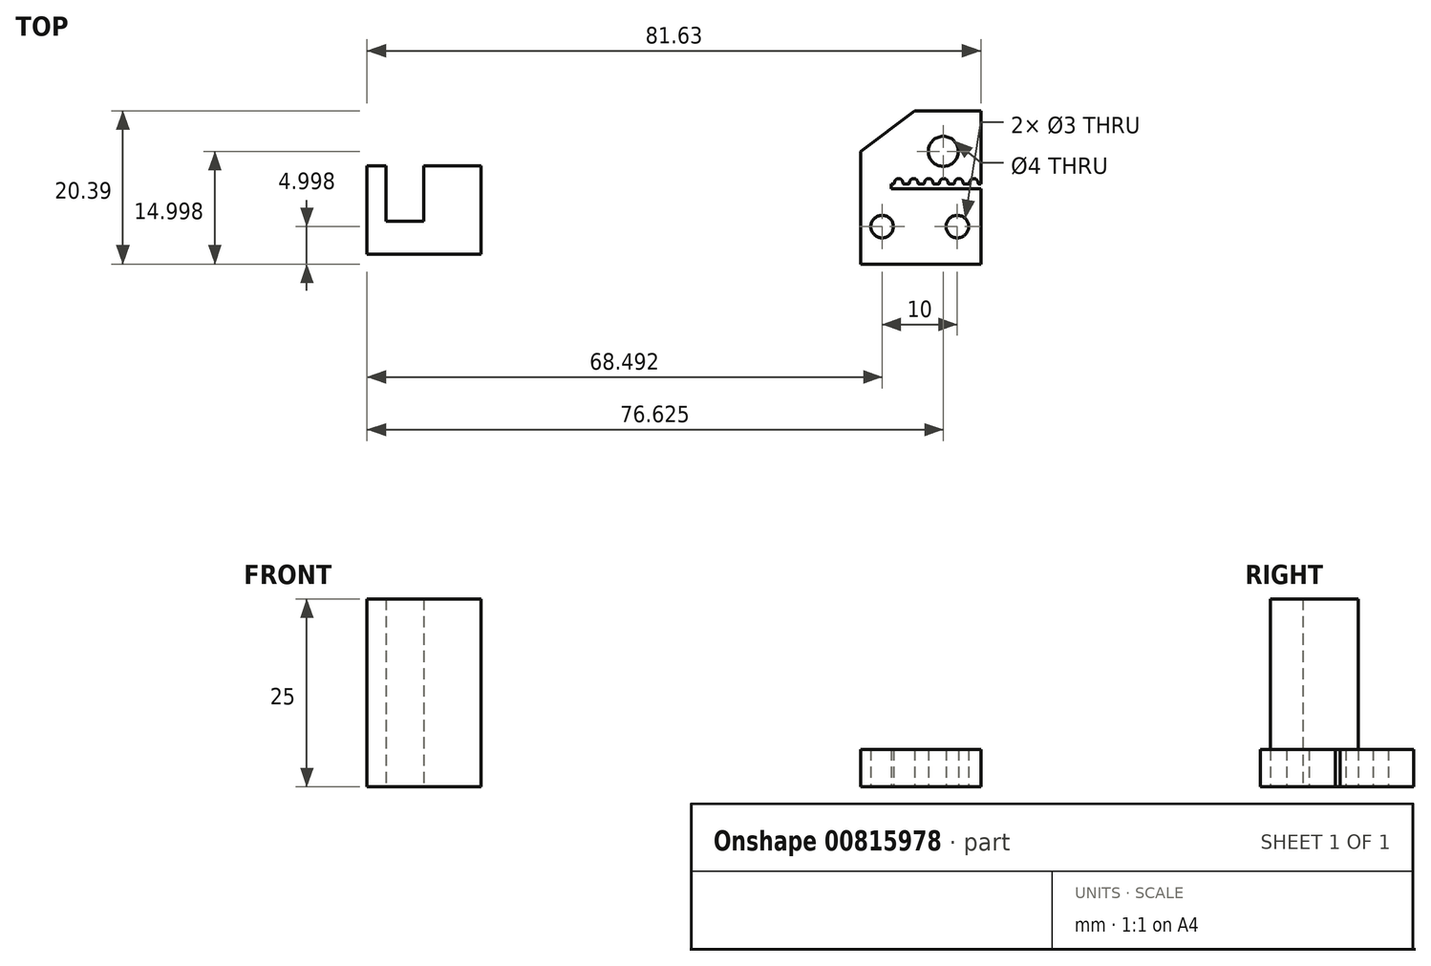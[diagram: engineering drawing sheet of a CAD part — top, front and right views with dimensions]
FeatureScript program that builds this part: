
annotation { "Feature Type Name" : "Feature", "Feature Type Description" : "" }
export const myFeature = defineFeature(function(context is Context, id is Id, definition is map)
    precondition{}
    {
        {
            var Q0;
            Q0=qCreatedBy(makeId("Top.planeOp"),FACE);
            var sketch = newSketch(context, id + "F0", { "sketchPlane" : qUnion([Q0])});
            skLineSegment(sketch, "E0.bottom", {"start": v(-41.36, 24.94) * mm, "end": v(38.64, 24.94) * mm});
            skLineSegment(sketch, "E0.top", {"start": v(-41.36, 74.94) * mm, "end": v(38.64, 74.94) * mm});
            skLineSegment(sketch, "E0.left", {"start": v(-41.36, 24.94) * mm, "end": v(-41.36, 74.94) * mm});
            skLineSegment(sketch, "E0.right", {"start": v(38.64, 24.94) * mm, "end": v(38.64, 74.94) * mm});
            skCircle(sketch, "E1", {"center": v(-21.36, 70.94) * mm, "radius": 1.37 * mm});
            skCircle(sketch, "E2", {"center": v(-21.36, 64.94) * mm, "radius": 1.5 * mm});
            skCircle(sketch, "E3", {"center": v(-11.36, 70.94) * mm, "radius": 1.5 * mm});
            skCircle(sketch, "E4", {"center": v(-11.36, 64.94) * mm, "radius": 1.5 * mm});
            skCircle(sketch, "E5", {"center": v(-1.36, 70.94) * mm, "radius": 1.5 * mm});
            skCircle(sketch, "E6", {"center": v(-1.36, 64.94) * mm, "radius": 1.5 * mm});
            skCircle(sketch, "E7", {"center": v(8.64, 70.94) * mm, "radius": 1.5 * mm});
            skCircle(sketch, "E8", {"center": v(8.64, 64.94) * mm, "radius": 1.5 * mm});
            skCircle(sketch, "E9", {"center": v(18.64, 70.94) * mm, "radius": 1.5 * mm});
            skCircle(sketch, "E10", {"center": v(18.64, 64.94) * mm, "radius": 1.5 * mm});
            skCircle(sketch, "E11", {"center": v(-21.36, 28.94) * mm, "radius": 1.5 * mm});
            skCircle(sketch, "E12", {"center": v(-11.36, 28.94) * mm, "radius": 1.5 * mm});
            skCircle(sketch, "E13", {"center": v(-1.36, 28.94) * mm, "radius": 1.5 * mm});
            skCircle(sketch, "E14", {"center": v(8.64, 28.94) * mm, "radius": 1.5 * mm});
            skCircle(sketch, "E15", {"center": v(18.64, 28.94) * mm, "radius": 1.5 * mm});
            skCircle(sketch, "E16", {"center": v(-11.36, 57.94) * mm, "radius": 1.5 * mm});
            skCircle(sketch, "E17", {"center": v(8.64, 57.94) * mm, "radius": 1.5 * mm});
            skCircle(sketch, "E18", {"center": v(-11.36, 37.94) * mm, "radius": 1.5 * mm});
            skCircle(sketch, "E19", {"center": v(8.64, 37.94) * mm, "radius": 1.5 * mm});
            skCircle(sketch, "E20", {"center": v(33.64, 62.94) * mm, "radius": 2 * mm});
            skCircle(sketch, "E21", {"center": v(35.5, 52.94) * mm, "radius": 1.5 * mm});
            skCircle(sketch, "E22", {"center": v(35.5, 42.94) * mm, "radius": 1.5 * mm});
            skCircle(sketch, "E23", {"center": v(25.5, 52.94) * mm, "radius": 1.5 * mm});
            skCircle(sketch, "E24", {"center": v(25.5, 42.94) * mm, "radius": 1.5 * mm});
            skCircle(sketch, "E25", {"center": v(33.84, 32.94) * mm, "radius": 2 * mm});
            skLineSegment(sketch, "E26", {"start": v(37.7, 57.94) * mm, "end": v(38.7, 57.94) * mm});
            skLineSegment(sketch, "E27", {"start": v(38.7, 57.94) * mm, "end": v(38.7, 58.57) * mm});
            skArc(sketch, "E28", {"start": v(38.2, 59) * mm, "mid": v(37.99, 59.23) * mm, "end": v(37.7, 59.32) * mm});
            skArc(sketch, "E29", {"start": v(38.29, 58.7) * mm, "mid": v(38.25, 58.86) * mm, "end": v(38.2, 59) * mm});
            skArc(sketch, "E30", {"start": v(38.29, 58.7) * mm, "mid": v(38.34, 58.6) * mm, "end": v(38.44, 58.57) * mm});
            skLineSegment(sketch, "E31", {"start": v(38.44, 58.57) * mm, "end": v(38.7, 58.57) * mm});
            skArc(sketch, "E32.0.MirrorCS", {"start": v(37.2, 59) * mm, "mid": v(37.4, 59.23) * mm, "end": v(37.7, 59.32) * mm});
            skArc(sketch, "E33.0.MirrorCS", {"start": v(37.1, 58.7) * mm, "mid": v(37.14, 58.86) * mm, "end": v(37.2, 59) * mm});
            skArc(sketch, "E34.0.MirrorCS", {"start": v(37.1, 58.7) * mm, "mid": v(37.05, 58.6) * mm, "end": v(36.96, 58.57) * mm});
            skLineSegment(sketch, "E35.0.MirrorCS", {"start": v(36.96, 58.57) * mm, "end": v(36.7, 58.57) * mm});
            skLineSegment(sketch, "E36.0.MirrorCS", {"start": v(36.7, 57.94) * mm, "end": v(36.7, 58.57) * mm});
            skLineSegment(sketch, "E37.0.MirrorCS", {"start": v(37.7, 57.94) * mm, "end": v(36.7, 57.94) * mm});
            skArc(sketch, "E38.MirrorCS", {"start": v(35.2, 59) * mm, "mid": v(35.4, 59.23) * mm, "end": v(35.7, 59.32) * mm});
            skArc(sketch, "E39.MirrorCS", {"start": v(36.2, 59) * mm, "mid": v(35.99, 59.23) * mm, "end": v(35.7, 59.32) * mm});
            skArc(sketch, "E40.MirrorCS", {"start": v(36.29, 58.7) * mm, "mid": v(36.25, 58.86) * mm, "end": v(36.2, 59) * mm});
            skArc(sketch, "E41.MirrorCS", {"start": v(36.29, 58.7) * mm, "mid": v(36.34, 58.6) * mm, "end": v(36.44, 58.57) * mm});
            skLineSegment(sketch, "E42.MirrorCS", {"start": v(36.44, 58.57) * mm, "end": v(36.7, 58.57) * mm});
            skArc(sketch, "E43.MirrorCS", {"start": v(35.1, 58.7) * mm, "mid": v(35.14, 58.86) * mm, "end": v(35.2, 59) * mm});
            skArc(sketch, "E44.MirrorCS", {"start": v(35.1, 58.7) * mm, "mid": v(35.05, 58.6) * mm, "end": v(34.96, 58.57) * mm});
            skLineSegment(sketch, "E45.MirrorCS", {"start": v(34.96, 58.57) * mm, "end": v(34.7, 58.57) * mm});
            skLineSegment(sketch, "E46.MirrorCS", {"start": v(34.7, 57.94) * mm, "end": v(34.7, 58.57) * mm});
            skLineSegment(sketch, "E47.MirrorCS", {"start": v(35.7, 57.94) * mm, "end": v(36.7, 57.94) * mm});
            skLineSegment(sketch, "E48.MirrorCS", {"start": v(35.7, 57.94) * mm, "end": v(34.7, 57.94) * mm});
            skLineSegment(sketch, "E49.MirrorCS", {"start": v(34.44, 58.57) * mm, "end": v(34.7, 58.57) * mm});
            skArc(sketch, "E50.MirrorCS", {"start": v(34.29, 58.7) * mm, "mid": v(34.34, 58.6) * mm, "end": v(34.44, 58.57) * mm});
            skArc(sketch, "E51.MirrorCS", {"start": v(34.29, 58.7) * mm, "mid": v(34.25, 58.86) * mm, "end": v(34.2, 59) * mm});
            skArc(sketch, "E52.MirrorCS", {"start": v(34.2, 59) * mm, "mid": v(33.99, 59.23) * mm, "end": v(33.7, 59.32) * mm});
            skArc(sketch, "E53.MirrorCS", {"start": v(33.2, 59) * mm, "mid": v(33.4, 59.23) * mm, "end": v(33.7, 59.32) * mm});
            skArc(sketch, "E54.MirrorCS", {"start": v(33.1, 58.7) * mm, "mid": v(33.14, 58.86) * mm, "end": v(33.2, 59) * mm});
            skArc(sketch, "E55.MirrorCS", {"start": v(33.1, 58.7) * mm, "mid": v(33.05, 58.6) * mm, "end": v(32.96, 58.57) * mm});
            skLineSegment(sketch, "E56.MirrorCS", {"start": v(32.96, 58.57) * mm, "end": v(32.7, 58.57) * mm});
            skLineSegment(sketch, "E57.MirrorCS", {"start": v(32.44, 58.57) * mm, "end": v(32.7, 58.57) * mm});
            skArc(sketch, "E58.MirrorCS", {"start": v(32.29, 58.7) * mm, "mid": v(32.34, 58.6) * mm, "end": v(32.44, 58.57) * mm});
            skArc(sketch, "E59.MirrorCS", {"start": v(32.29, 58.7) * mm, "mid": v(32.25, 58.86) * mm, "end": v(32.2, 59) * mm});
            skArc(sketch, "E60.MirrorCS", {"start": v(32.2, 59) * mm, "mid": v(31.99, 59.23) * mm, "end": v(31.7, 59.32) * mm});
            skArc(sketch, "E61.MirrorCS", {"start": v(31.2, 59) * mm, "mid": v(31.4, 59.23) * mm, "end": v(31.7, 59.32) * mm});
            skArc(sketch, "E62.MirrorCS", {"start": v(31.1, 58.7) * mm, "mid": v(31.14, 58.86) * mm, "end": v(31.2, 59) * mm});
            skArc(sketch, "E63.MirrorCS", {"start": v(31.1, 58.7) * mm, "mid": v(31.05, 58.6) * mm, "end": v(30.96, 58.57) * mm});
            skLineSegment(sketch, "E64.MirrorCS", {"start": v(30.96, 58.57) * mm, "end": v(30.7, 58.57) * mm});
            skLineSegment(sketch, "E65.MirrorCS", {"start": v(30.7, 57.94) * mm, "end": v(30.7, 58.57) * mm});
            skLineSegment(sketch, "E66.MirrorCS", {"start": v(31.7, 57.94) * mm, "end": v(30.7, 57.94) * mm});
            skLineSegment(sketch, "E67.MirrorCS", {"start": v(31.7, 57.94) * mm, "end": v(32.7, 57.94) * mm});
            skLineSegment(sketch, "E68.MirrorCS", {"start": v(33.7, 57.94) * mm, "end": v(32.7, 57.94) * mm});
            skLineSegment(sketch, "E69.MirrorCS", {"start": v(33.7, 57.94) * mm, "end": v(34.7, 57.94) * mm});
            skLineSegment(sketch, "E70.MirrorCS", {"start": v(29.7, 57.94) * mm, "end": v(30.7, 57.94) * mm});
            skLineSegment(sketch, "E71.MirrorCS", {"start": v(29.7, 57.94) * mm, "end": v(28.7, 57.94) * mm});
            skLineSegment(sketch, "E72.MirrorCS", {"start": v(27.7, 57.94) * mm, "end": v(28.7, 57.94) * mm});
            skLineSegment(sketch, "E73.MirrorCS", {"start": v(27.7, 57.94) * mm, "end": v(26.7, 57.94) * mm});
            skLineSegment(sketch, "E74.MirrorCS", {"start": v(26.7, 57.94) * mm, "end": v(26.7, 58.57) * mm});
            skLineSegment(sketch, "E75.MirrorCS", {"start": v(30.44, 58.57) * mm, "end": v(30.7, 58.57) * mm});
            skArc(sketch, "E76.MirrorCS", {"start": v(30.29, 58.7) * mm, "mid": v(30.34, 58.6) * mm, "end": v(30.44, 58.57) * mm});
            skArc(sketch, "E77.MirrorCS", {"start": v(30.29, 58.7) * mm, "mid": v(30.25, 58.86) * mm, "end": v(30.2, 59) * mm});
            skArc(sketch, "E78.MirrorCS", {"start": v(30.2, 59) * mm, "mid": v(29.99, 59.23) * mm, "end": v(29.7, 59.32) * mm});
            skArc(sketch, "E79.MirrorCS", {"start": v(29.2, 59) * mm, "mid": v(29.4, 59.23) * mm, "end": v(29.7, 59.32) * mm});
            skArc(sketch, "E80.MirrorCS", {"start": v(29.1, 58.7) * mm, "mid": v(29.14, 58.86) * mm, "end": v(29.2, 59) * mm});
            skArc(sketch, "E81.MirrorCS", {"start": v(29.1, 58.7) * mm, "mid": v(29.05, 58.6) * mm, "end": v(28.96, 58.57) * mm});
            skLineSegment(sketch, "E82.MirrorCS", {"start": v(28.96, 58.57) * mm, "end": v(28.7, 58.57) * mm});
            skLineSegment(sketch, "E83.MirrorCS", {"start": v(28.44, 58.57) * mm, "end": v(28.7, 58.57) * mm});
            skArc(sketch, "E84.MirrorCS", {"start": v(28.29, 58.7) * mm, "mid": v(28.34, 58.6) * mm, "end": v(28.44, 58.57) * mm});
            skArc(sketch, "E85.MirrorCS", {"start": v(28.29, 58.7) * mm, "mid": v(28.25, 58.86) * mm, "end": v(28.2, 59) * mm});
            skArc(sketch, "E86.MirrorCS", {"start": v(28.2, 59) * mm, "mid": v(27.99, 59.23) * mm, "end": v(27.7, 59.32) * mm});
            skArc(sketch, "E87.MirrorCS", {"start": v(27.2, 59) * mm, "mid": v(27.4, 59.23) * mm, "end": v(27.7, 59.32) * mm});
            skArc(sketch, "E88.MirrorCS", {"start": v(27.1, 58.7) * mm, "mid": v(27.14, 58.86) * mm, "end": v(27.2, 59) * mm});
            skArc(sketch, "E89.MirrorCS", {"start": v(27.1, 58.7) * mm, "mid": v(27.05, 58.6) * mm, "end": v(26.96, 58.57) * mm});
            skLineSegment(sketch, "E90.MirrorCS", {"start": v(26.96, 58.57) * mm, "end": v(26.7, 58.57) * mm});
            skPoint(sketch, "E91", {"position": v(38.64, 47.94) * mm});
            skLineSegment(sketch, "E92", {"start": v(38.64, 47.94) * mm, "end": v(22.64, 47.94) * mm});
            skLineSegment(sketch, "E93", {"start": v(22.64, 47.94) * mm, "end": v(22.64, 62.94) * mm});
            skLineSegment(sketch, "E94", {"start": v(22.64, 62.94) * mm, "end": v(38.64, 74.94) * mm});
            skLineSegment(sketch, "E95", {"start": v(29.83, 68.33) * mm, "end": v(38.64, 68.33) * mm});
            skSolve(sketch);
        }
        {
            var Q0;
            Q0=makeQuery(id+"F0.imprint","IMPRINT",FACE,{"disambiguationData":[TD([[makeQuery(id+"F0.imprint","IMPRINT",EDGE,{"derivedFrom":sQuery(id+"F0.wireOp",EDGE,"E20")}),-1.0]])]});
            extrude(context, id + "F1", {"entities" : qUnion([Q0]), "depth" : 5 * mm, "offsetDistance" : 25 * mm});
        }
        {
            var Q0;
            Q0=qCreatedBy(makeId("Top.planeOp"),FACE);
            var sketch = newSketch(context, id + "F2", { "sketchPlane" : qUnion([Q0])});
            skLineSegment(sketch, "E96.bottom", {"start": v(-42.99, 60.98) * mm, "end": v(-27.85, 60.98) * mm});
            skLineSegment(sketch, "E96.top", {"start": v(-42.99, 49.3) * mm, "end": v(-27.85, 49.3) * mm});
            skLineSegment(sketch, "E96.left", {"start": v(-42.99, 60.98) * mm, "end": v(-42.99, 49.3) * mm});
            skLineSegment(sketch, "E96.right", {"start": v(-27.85, 60.98) * mm, "end": v(-27.85, 49.3) * mm});
            skPoint(sketch, "E97.oppositeSnap0", {"position": v(-35.42, 60.98) * mm});
            skLineSegment(sketch, "E97.bottom", {"start": v(-40.5, 60.98) * mm, "end": v(-35.42, 60.98) * mm});
            skLineSegment(sketch, "E97.top", {"start": v(-40.5, 53.62) * mm, "end": v(-35.42, 53.62) * mm});
            skLineSegment(sketch, "E97.left", {"start": v(-40.5, 60.98) * mm, "end": v(-40.5, 53.62) * mm});
            skLineSegment(sketch, "E97.right", {"start": v(-35.42, 60.98) * mm, "end": v(-35.42, 53.62) * mm});
            skSolve(sketch);
        }
        {
            var Q0;
            Q0=makeQuery(id+"F2.imprint","IMPRINT",FACE,{"disambiguationData":[TD([[makeQuery(id+"F2.imprint","IMPRINT",EDGE,{"derivedFrom":sQuery(id+"F2.wireOp",EDGE,"E96.top")}),1.0]])]});
            extrude(context, id + "F3", {"entities" : qUnion([Q0]), "depth" : 25 * mm, "offsetDistance" : 25 * mm});
        }
    });
